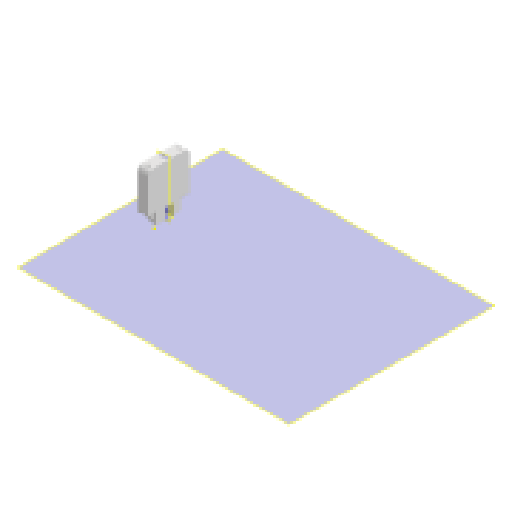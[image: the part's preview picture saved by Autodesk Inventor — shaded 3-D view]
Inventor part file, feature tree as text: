
AUTODESK INVENTOR PART (.ipt)
format: ipt  version: 2024.1 (Build 281209000, 209)  size: 207,360 bytes
history: native  units: mm
features: sketch x5, extrude x4, reference x4, plane x3, fillet x3, other x3, projected_geometry x2, mirror x1
ambient origin geometry x8: Origin, YZ Plane, XZ Plane, XY Plane, X Axis, Y Axis, Z Axis, Center Point
bodies: Volumenkörper1 (feature_tree)
feature tree (25):
  plane  "Arbeitsebene1"
  extrude  "Extrusion1"  Depth=10.0mm
  fillet  "Rundung1"  Radius=50.0mm
  extrude  "Extrusion2"  Depth=0.5mm
  plane  "Arbeitsebene2"
  extrude  "Extrusion3"  Depth=7.8mm TaperAngle=0.0deg
  plane  "Arbeitsebene3"
  extrude  "Extrusion4"  Depth=10.0mm TaperAngle=0.0deg
  fillet  "Fillet4"  Radius=1.0mm
  mirror  "Spiegeln1"
  fillet  "Rundung3"  [1 undecoded]
  sketch  "Skizze6"
  sketch  "Skizze1"  dims[d0=10.0mm d1=40.0mm d2=50.0mm d3=0.0mm]
  reference  "Referenz1"
  sketch  "Skizze2"  dims[d4=5.0mm d5=0.5mm]
  reference  "Referenz2"
  reference  "Referenz3"
  projected_geometry  "Projizierte Kontur1"
  sketch  "Skizze3"  dims[d6=40.0mm d7=0.0mm d8=7.8mm d9=0.0mm]
  reference  "Referenz4"
  projected_geometry  "Projizierte Kontur2"
  sketch  "Sketch5"  dims[d11=2.0mm d12=10.0mm d13=0.0mm d14=1.0mm]
  other  "Assembly_Planktoscope_Uc2version_wormdrive_V3.iam"
  other  "60_Planktoscope_MicroscopeHolder_Bottom_v0:1"
  other  "60_Planktoscope_Illuminationsource:1"
note: 1 required parameter value undecoded (feature->parameter linkage not recoverable at this tier; creation-order binding heuristic only, values carry confidence <= 0.55)
